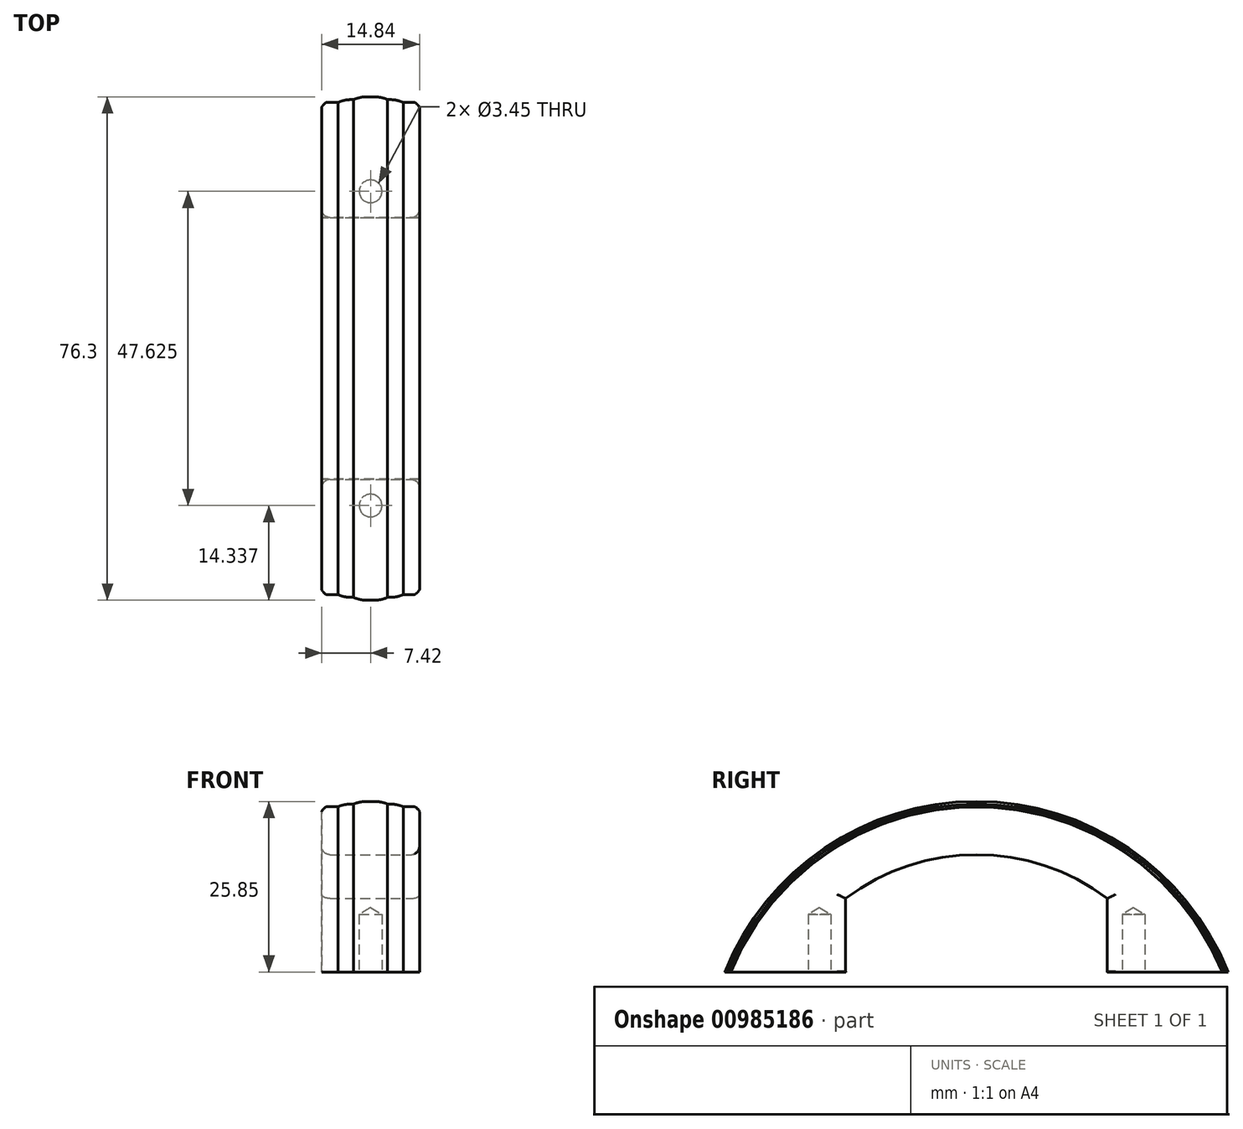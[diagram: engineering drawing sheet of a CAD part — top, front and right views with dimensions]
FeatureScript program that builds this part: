
annotation { "Feature Type Name" : "Feature", "Feature Type Description" : "" }
export const myFeature = defineFeature(function(context is Context, id is Id, definition is map)
    precondition{}
    {
        {
            var Q0;
            Q0=qCreatedBy(makeId("Front.planeOp"),FACE);
            var sketch = newSketch(context, id + "F0", { "sketchPlane" : qUnion([Q0])});
            skLineSegment(sketch, "E0", {"start": v(-55.67, 0) * mm, "end": v(68.03, 0) * mm, "construction": true});
            skLineSegment(sketch, "E1", {"start": v(-7.42, 0) * mm, "end": v(-7.42, 40.28) * mm});
            skLineSegment(sketch, "E2", {"start": v(-7.42, 40.28) * mm, "end": v(-4.96, 40.28) * mm});
            skLineSegment(sketch, "E3", {"start": v(-4.96, 40.28) * mm, "end": v(-4.96, 40.68) * mm});
            skLineSegment(sketch, "E4", {"start": v(-4.96, 40.68) * mm, "end": v(-2.58, 40.68) * mm});
            skLineSegment(sketch, "E5", {"start": v(-2.58, 40.68) * mm, "end": v(-2.58, 41.08) * mm});
            skLineSegment(sketch, "E6", {"start": v(-2.58, 41.08) * mm, "end": v(2.58, 41.08) * mm});
            skLineSegment(sketch, "E7", {"start": v(2.58, 41.08) * mm, "end": v(2.58, 40.68) * mm});
            skLineSegment(sketch, "E8", {"start": v(2.58, 40.68) * mm, "end": v(4.96, 40.68) * mm});
            skLineSegment(sketch, "E9", {"start": v(4.96, 40.68) * mm, "end": v(4.96, 40.28) * mm});
            skLineSegment(sketch, "E10", {"start": v(4.96, 40.28) * mm, "end": v(7.42, 40.28) * mm});
            skLineSegment(sketch, "E11", {"start": v(7.42, 40.28) * mm, "end": v(7.42, 0) * mm});
            skLineSegment(sketch, "E12", {"start": v(7.42, 0) * mm, "end": v(-7.42, 0) * mm});
            skLineSegment(sketch, "E13", {"start": v(0, 0) * mm, "end": v(0, 47.43) * mm, "construction": true});
            skSolve(sketch);
        }
        {
            var Q0;
            Q0=makeQuery(id+"F0.imprint","IMPRINT",FACE,{"disambiguationData":[TD([[makeQuery(id+"F0.imprint","IMPRINT",EDGE,{"derivedFrom":sQuery(id+"F0.wireOp",EDGE,"E1")}),-1.0]])]});
            var Q1;
            Q1=sQuery(id+"F0.wireOp",EDGE,"E0");
            revolve(context, id + "F1", {"surfaceOperationType" : NewSurfaceOperationType.NEW, "entities" : qUnion([Q0]), "axis" : qUnion([Q1]), "revolveType" : RevolveType.FULL});
        }
        {
            var Q0;
            Q0=makeQuery(id+"F1.opRevolve","SWEPT_EDGE",EDGE,{"disambiguationData":[OSD([sQuery(id+"F0.wireOp",EDGE,"E10"),sQuery(id+"F0.wireOp",EDGE,"E11")])]});
            var Q1;
            Q1=makeQuery(id+"F1.opRevolve","SWEPT_EDGE",EDGE,{"disambiguationData":[OSD([sQuery(id+"F0.wireOp",EDGE,"E1"),sQuery(id+"F0.wireOp",EDGE,"E2")])]});
            fillet(context, id + "F2", {"entities" : qUnion([Q0, Q1]), "radius" : 0.76 * mm, "tangentPropagation" : true, "rho" : 0.2, "crossSection" : FilletCrossSection.CONIC, "allowEdgeOverflow" : false});
        }
        {
            var Q0;
            Q0=makeQuery(id+"F1.opRevolve","SWEPT_EDGE",EDGE,{"disambiguationData":[OSD([sQuery(id+"F0.wireOp",EDGE,"E8"),sQuery(id+"F0.wireOp",EDGE,"E9")])]});
            var Q1;
            Q1=makeQuery(id+"F1.opRevolve","SWEPT_EDGE",EDGE,{"disambiguationData":[OSD([sQuery(id+"F0.wireOp",EDGE,"E3"),sQuery(id+"F0.wireOp",EDGE,"E4")])]});
            fillet(context, id + "F3", {"entities" : qUnion([Q0, Q1]), "radius" : 5.08 * mm, "tangentPropagation" : true, "allowEdgeOverflow" : false});
        }
        {
            var Q0;
            Q0=makeQuery(id+"F1.opRevolve","SWEPT_EDGE",EDGE,{"disambiguationData":[OSD([sQuery(id+"F0.wireOp",EDGE,"E6"),sQuery(id+"F0.wireOp",EDGE,"E7")])]});
            var Q1;
            Q1=makeQuery(id+"F1.opRevolve","SWEPT_EDGE",EDGE,{"disambiguationData":[OSD([sQuery(id+"F0.wireOp",EDGE,"E5"),sQuery(id+"F0.wireOp",EDGE,"E6")])]});
            fillet(context, id + "F4", {"entities" : qUnion([Q0, Q1]), "radius" : 5.08 * mm, "tangentPropagation" : true, "allowEdgeOverflow" : false});
        }
        {
            var Q0;
            Q0=qCreatedBy(makeId("Right.planeOp"),FACE);
            var sketch = newSketch(context, id + "F5", { "sketchPlane" : qUnion([Q0])});
            skCircle(sketch, "E14", {"center": v(0, 0) * mm, "radius": 25 * mm});
            skSolve(sketch);
        }
        {
            var Q0;
            Q0=qSketchRegion(id+"F5",true);
            extrude(context, id + "F6", {"entities" : qUnion([Q0]), "operationType" : NewBodyOperationType.REMOVE, "endBound" : BoundingType.THROUGH_ALL, "depth" : 25.4 * mm, "offsetDistance" : 25.4 * mm, "hasSecondDirection" : true, "secondDirectionBound" : SecondDirectionBoundingType.THROUGH_ALL, "secondDirectionOppositeDirection" : true, "secondDirectionDepth" : 25.4 * mm});
        }
        {
            var Q0;
            Q0=qCreatedBy(makeId("Right.planeOp"),FACE);
            var sketch = newSketch(context, id + "F7", { "sketchPlane" : qUnion([Q0])});
            skLineSegment(sketch, "E15", {"start": v(0, 15.23) * mm, "end": v(-38.1, 15.23) * mm, "construction": true});
            skLineSegment(sketch, "E16.MirrorCS", {"start": v(0, 15.23) * mm, "end": v(38.1, 15.23) * mm, "construction": true});
            skLineSegment(sketch, "E17", {"start": v(-59.25, 15.23) * mm, "end": v(65.7, 15.23) * mm});
            skLineSegment(sketch, "E18", {"start": v(65.7, 15.23) * mm, "end": v(65.7, -43.9) * mm});
            skLineSegment(sketch, "E19", {"start": v(65.7, -43.9) * mm, "end": v(-59.25, -43.9) * mm});
            skLineSegment(sketch, "E20", {"start": v(-59.25, -43.9) * mm, "end": v(-59.25, 15.23) * mm});
            skSolve(sketch);
        }
        {
            var Q0;
            Q0=qSketchRegion(id+"F7",true);
            extrude(context, id + "F8", {"entities" : qUnion([Q0]), "operationType" : NewBodyOperationType.REMOVE, "endBound" : BoundingType.THROUGH_ALL, "oppositeDirection" : true, "depth" : 25.4 * mm, "offsetDistance" : 25.4 * mm, "hasSecondDirection" : true, "secondDirectionBound" : SecondDirectionBoundingType.THROUGH_ALL, "secondDirectionOppositeDirection" : false, "secondDirectionDepth" : 25.4 * mm});
        }
        {
            var Q0;
            Q0=qCreatedBy(makeId("Right.planeOp"),FACE);
            var sketch = newSketch(context, id + "F9", { "sketchPlane" : qUnion([Q0])});
            skLineSegment(sketch, "E21", {"start": v(-19.86, 15.26) * mm, "end": v(-19.86, 26.38) * mm});
            skLineSegment(sketch, "E22.MirrorCS", {"start": v(19.86, 15.26) * mm, "end": v(19.86, 26.38) * mm});
            skArc(sketch, "E23", {"start": v(-19.86, 26.38) * mm, "mid": v(0, 33.01) * mm, "end": v(19.86, 26.38) * mm});
            skLineSegment(sketch, "E24", {"start": v(-19.86, 15.26) * mm, "end": v(19.86, 15.26) * mm});
            skSolve(sketch);
        }
        {
            var Q0;
            Q0=qSketchRegion(id+"F9",true);
            extrude(context, id + "F10", {"entities" : qUnion([Q0]), "operationType" : NewBodyOperationType.REMOVE, "endBound" : BoundingType.THROUGH_ALL, "oppositeDirection" : true, "depth" : 25.4 * mm, "offsetDistance" : 25.4 * mm, "hasSecondDirection" : true, "secondDirectionBound" : SecondDirectionBoundingType.THROUGH_ALL, "secondDirectionOppositeDirection" : false, "secondDirectionDepth" : 25.4 * mm});
        }
        {
            var Q0;
            Q0=makeQuery(id+"F10.boolean.opBoolean","INTERSECT",EDGE,{"derivedFrom":[makeQuery(id+"F1.opRevolve","SWEPT_FACE",FACE,{"disambiguationData":[OSD([sQuery(id+"F0.wireOp",EDGE,"E11")])]}),makeQuery(id+"F10.opExtrude","SWEPT_FACE",FACE,{"disambiguationData":[OSD([sQuery(id+"F9.wireOp",EDGE,"E23")])]})]});
            var Q1;
            Q1=makeQuery(id+"F10.boolean.opBoolean","INTERSECT",EDGE,{"derivedFrom":[makeQuery(id+"F1.opRevolve","SWEPT_FACE",FACE,{"disambiguationData":[OSD([sQuery(id+"F0.wireOp",EDGE,"E11")])]}),makeQuery(id+"F10.opExtrude","SWEPT_FACE",FACE,{"disambiguationData":[OSD([sQuery(id+"F9.wireOp",EDGE,"E21")])]})]});
            var Q2;
            Q2=makeQuery(id+"F10.boolean.opBoolean","INTERSECT",EDGE,{"derivedFrom":[makeQuery(id+"F1.opRevolve","SWEPT_FACE",FACE,{"disambiguationData":[OSD([sQuery(id+"F0.wireOp",EDGE,"E11")])]}),makeQuery(id+"F10.opExtrude","SWEPT_FACE",FACE,{"disambiguationData":[OSD([sQuery(id+"F9.wireOp",EDGE,"E22.MirrorCS")])]})]});
            var Q3;
            Q3=makeQuery(id+"F10.boolean.opBoolean","INTERSECT",EDGE,{"derivedFrom":[makeQuery(id+"F1.opRevolve","SWEPT_FACE",FACE,{"disambiguationData":[OSD([sQuery(id+"F0.wireOp",EDGE,"E1")])]}),makeQuery(id+"F10.opExtrude","SWEPT_FACE",FACE,{"disambiguationData":[OSD([sQuery(id+"F9.wireOp",EDGE,"E23")])]})]});
            var Q4;
            Q4=makeQuery(id+"F10.boolean.opBoolean","INTERSECT",EDGE,{"derivedFrom":[makeQuery(id+"F1.opRevolve","SWEPT_FACE",FACE,{"disambiguationData":[OSD([sQuery(id+"F0.wireOp",EDGE,"E1")])]}),makeQuery(id+"F10.opExtrude","SWEPT_FACE",FACE,{"disambiguationData":[OSD([sQuery(id+"F9.wireOp",EDGE,"E21")])]})]});
            var Q5;
            Q5=makeQuery(id+"F10.boolean.opBoolean","INTERSECT",EDGE,{"derivedFrom":[makeQuery(id+"F1.opRevolve","SWEPT_FACE",FACE,{"disambiguationData":[OSD([sQuery(id+"F0.wireOp",EDGE,"E1")])]}),makeQuery(id+"F10.opExtrude","SWEPT_FACE",FACE,{"disambiguationData":[OSD([sQuery(id+"F9.wireOp",EDGE,"E22.MirrorCS")])]})]});
            fillet(context, id + "F11", {"entities" : qUnion([Q0, Q1, Q2, Q3, Q4, Q5]), "radius" : 1.27 * mm, "tangentPropagation" : true, "allowEdgeOverflow" : false});
        }
        {
            var Q0;
            Q0=qCreatedBy(makeId("Top.planeOp"),FACE);
            var sketch = newSketch(context, id + "F12", { "sketchPlane" : qUnion([Q0])});
            skLineSegment(sketch, "E25", {"start": v(-14.34, 23.81) * mm, "end": v(15.86, 23.81) * mm, "construction": true});
            skLineSegment(sketch, "E26.MirrorCS", {"start": v(-14.34, -23.81) * mm, "end": v(15.86, -23.81) * mm, "construction": true});
            skPoint(sketch, "E27", {"position": v(0, 23.81) * mm});
            skPoint(sketch, "E28", {"position": v(0, -23.81) * mm});
            skSolve(sketch);
        }
        {
            var Q0;
            Q0=sQuery(id+"F12.wireOp",VERTEX,"E28");
            var Q1;
            Q1=sQuery(id+"F12.wireOp",VERTEX,"E27");
            var Q2;
            Q2=makeQuery(id+"F1.opRevolve","SWEPT_BODY",BODY,{"disambiguationData":[OSD([sQuery(id+"F0.wireOp",EDGE,"E1"),sQuery(id+"F0.wireOp",EDGE,"E2"),sQuery(id+"F0.wireOp",EDGE,"E3"),sQuery(id+"F0.wireOp",EDGE,"E4"),sQuery(id+"F0.wireOp",EDGE,"E5"),sQuery(id+"F0.wireOp",EDGE,"E6"),sQuery(id+"F0.wireOp",EDGE,"E7"),sQuery(id+"F0.wireOp",EDGE,"E8"),sQuery(id+"F0.wireOp",EDGE,"E9"),sQuery(id+"F0.wireOp",EDGE,"E10"),sQuery(id+"F0.wireOp",EDGE,"E11"),sQuery(id+"F0.wireOp",EDGE,"E12")])]});
            hole(context, id + "F13", {"style" : HoleStyle.SIMPLE, "endStyle" : HoleEndStyle.BLIND, "oppositeDirection" : true, "standardTappedOrClearance" : lookupTablePath({ "standard" : "ANSI", "engagement" : "75%", "pitch" : "32 tpi", "size" : "#8", "type" : "Tapped" }), "standardBlindInLast" : lookupTablePath({ "standard" : "ANSI", "fit" : "Normal", "engagement" : "75%", "pitch" : "32 tpi", "size" : "#8", "type" : "Clearance & tapped" }), "holeDiameter" : 3.45 * mm, "majorDiameter" : 4.17 * mm, "showTappedDepth" : true, "holeDepth" : 23.97 * mm, "isTappedThrough" : true, "tappedDepth" : 21.59 * mm, "tapClearance" : 3, "startFromSketch" : true, "locations" : qUnion([Q0, Q1]), "scope" : qUnion([Q2])});
        }
    });
